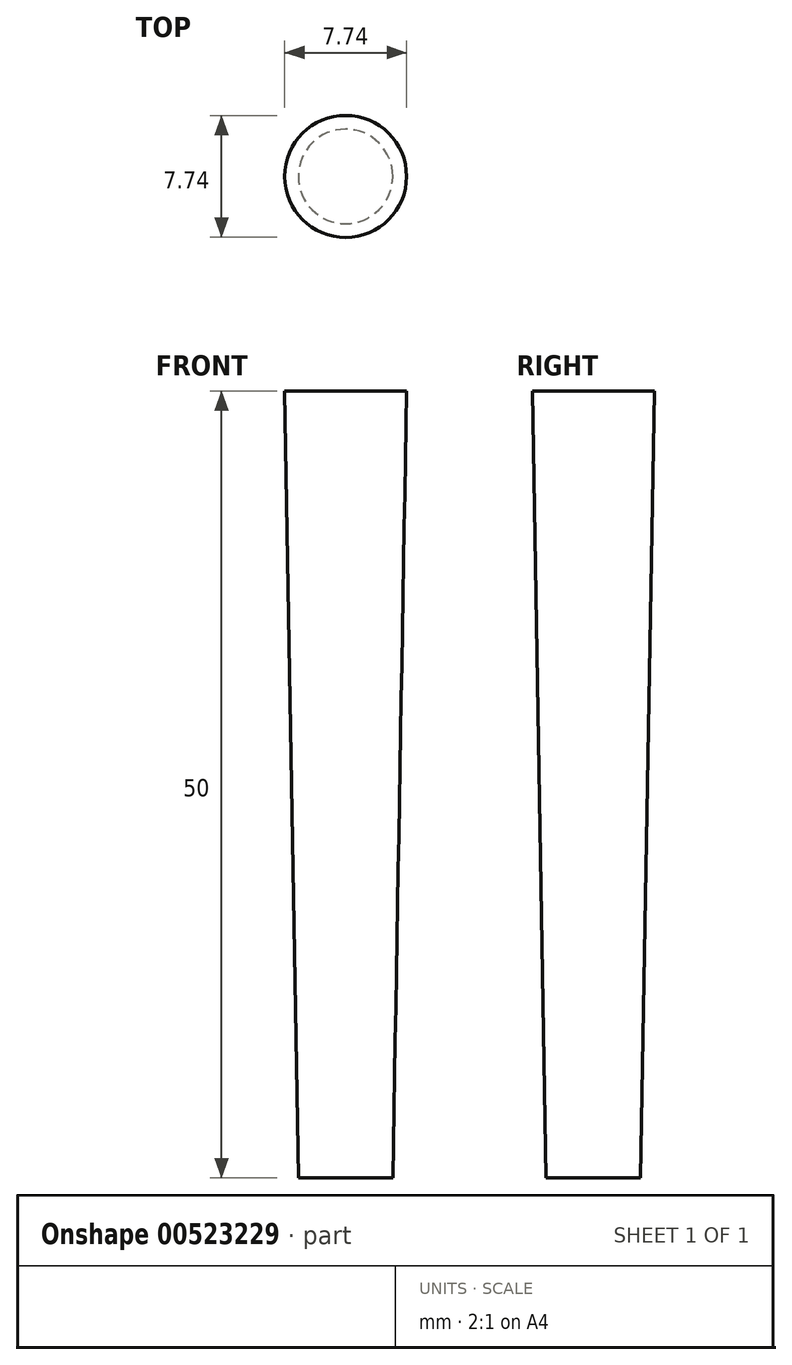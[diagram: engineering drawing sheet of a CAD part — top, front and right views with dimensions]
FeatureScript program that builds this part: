
annotation { "Feature Type Name" : "Feature", "Feature Type Description" : "" }
export const myFeature = defineFeature(function(context is Context, id is Id, definition is map)
    precondition{}
    {
        {
            var Q0;
            Q0=qCreatedBy(makeId("Top.planeOp"),FACE);
            var sketch = newSketch(context, id + "F0", { "sketchPlane" : qUnion([Q0])});
            skCircle(sketch, "E0", {"center": v(0, 0) * mm, "radius": 3 * mm});
            skSolve(sketch);
        }
        {
            var Q0;
            Q0 = qSketchRegion(id + "F0", true);
            extrude(context, id + "F1", {"entities" : qUnion([Q0]), "depth" : 50 * mm, "offsetDistance" : 25 * mm, "hasDraft" : true, "draftAngle" : 1 * degree});
        }
    });
